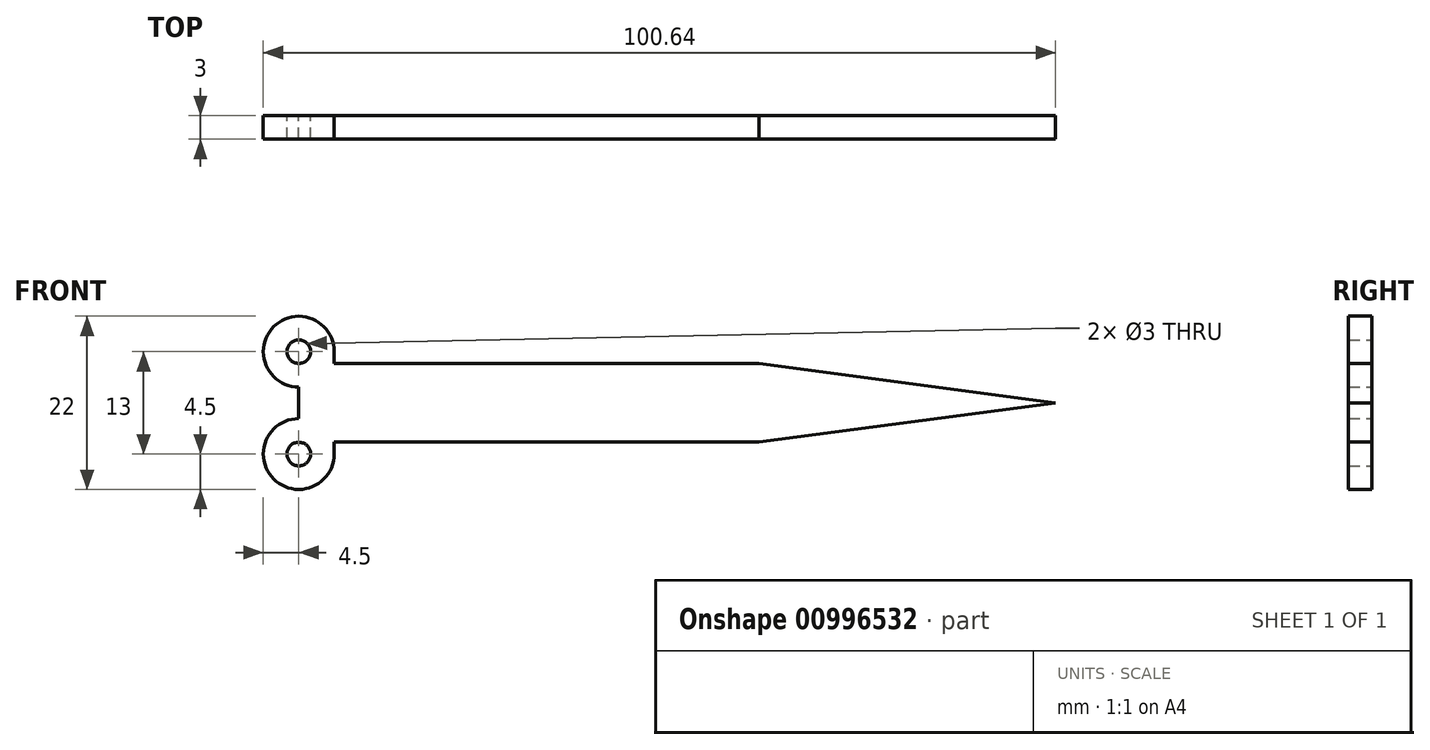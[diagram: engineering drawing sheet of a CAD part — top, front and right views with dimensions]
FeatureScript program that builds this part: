
annotation { "Feature Type Name" : "Feature", "Feature Type Description" : "" }
export const myFeature = defineFeature(function(context is Context, id is Id, definition is map)
    precondition{}
    {
        {
            var Q0;
            Q0=qCreatedBy(makeId("Front.planeOp"),FACE);
            var sketch = newSketch(context, id + "F0", { "sketchPlane" : qUnion([Q0])});
            skCircle(sketch, "E0", {"center": v(-28, 1.6) * mm, "radius": 1.5 * mm});
            skCircle(sketch, "E1", {"center": v(-28, 1.6) * mm, "radius": 4.5 * mm});
            skLineSegment(sketch, "E2", {"start": v(-23.5, 1.6) * mm, "end": v(-23.5, -4.9) * mm});
            skLineSegment(sketch, "E3", {"start": v(68.14, -4.9) * mm, "end": v(30.47, 0.1) * mm});
            skLineSegment(sketch, "E4", {"start": v(30.47, 0.1) * mm, "end": v(-23.5, 0.1) * mm});
            skCircle(sketch, "E5.MirrorC", {"center": v(-28, -11.4) * mm, "radius": 4.5 * mm});
            skLineSegment(sketch, "E6.MirrorCS", {"start": v(-23.5, -11.4) * mm, "end": v(-23.5, -4.9) * mm});
            skLineSegment(sketch, "E7.MirrorCS", {"start": v(30.47, -9.9) * mm, "end": v(-23.5, -9.9) * mm});
            skLineSegment(sketch, "E8.MirrorCS", {"start": v(68.14, -4.9) * mm, "end": v(30.47, -9.9) * mm});
            skCircle(sketch, "E9.MirrorC", {"center": v(-28, -11.4) * mm, "radius": 1.5 * mm});
            skLineSegment(sketch, "E10", {"start": v(-28, -4.9) * mm, "end": v(-28, -6.9) * mm});
            skLineSegment(sketch, "E11", {"start": v(-28, 1.6) * mm, "end": v(-28, -11.4) * mm});
            skSolve(sketch);
        }
        {
            var Q0;
            Q0 = qSketchRegion(id + "F0", true);
            extrude(context, id + "F1", {"entities" : qUnion([Q0]), "endBound" : BoundingType.SYMMETRIC, "depth" : 3 * mm, "offsetDistance" : 25 * mm});
        }
    });
